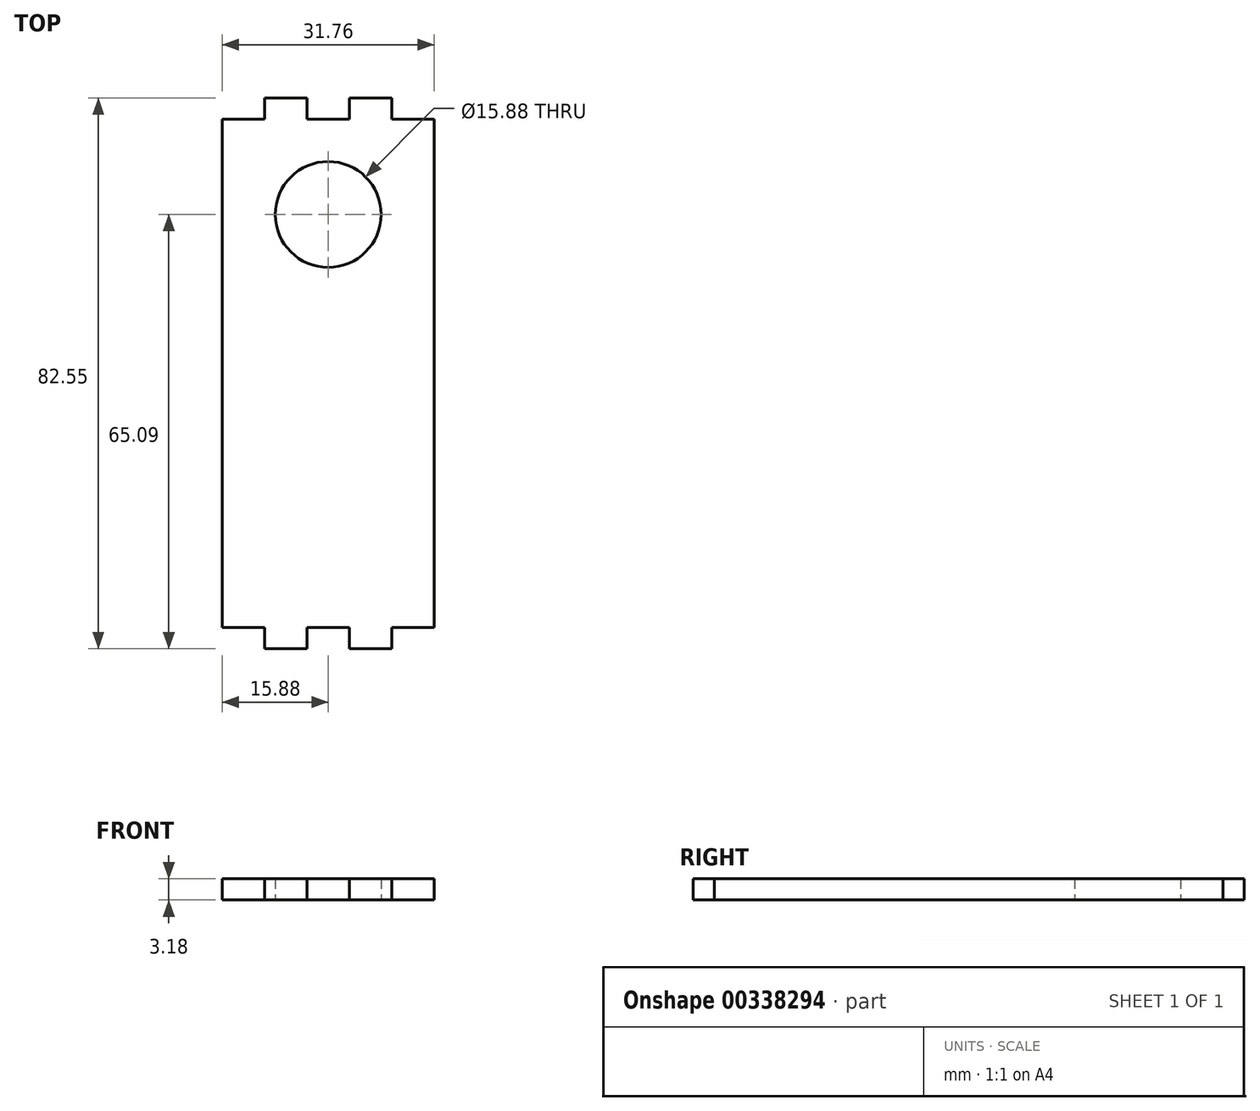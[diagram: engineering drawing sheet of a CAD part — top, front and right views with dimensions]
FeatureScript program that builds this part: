
annotation { "Feature Type Name" : "Feature", "Feature Type Description" : "" }
export const myFeature = defineFeature(function(context is Context, id is Id, definition is map)
    precondition{}
    {
        {
            var Q0;
            Q0=qCreatedBy(makeId("Top.planeOp"),FACE);
            var sketch = newSketch(context, id + "F0", { "sketchPlane" : qUnion([Q0])});
            skCircle(sketch, "E0", {"center": v(0, 0) * mm, "radius": 7.94 * mm});
            skLineSegment(sketch, "E1.bottom", {"start": v(-15.87, 17.46) * mm, "end": v(15.87, 17.46) * mm});
            skLineSegment(sketch, "E1.top", {"start": v(-15.87, -65.09) * mm, "end": v(15.87, -65.09) * mm});
            skLineSegment(sketch, "E1.left", {"start": v(-15.88, 17.46) * mm, "end": v(-15.87, -65.09) * mm});
            skLineSegment(sketch, "E1.right", {"start": v(15.88, 17.46) * mm, "end": v(15.88, -65.09) * mm});
            skLineSegment(sketch, "E2", {"start": v(0, 0) * mm, "end": v(0, 17.46) * mm, "construction": true});
            skSolve(sketch);
        }
        {
            var Q0;
            Q0=makeQuery(id+"F0.imprint","IMPRINT",FACE,{"disambiguationData":[TD([[makeQuery(id+"F0.imprint","IMPRINT",EDGE,{"derivedFrom":sQuery(id+"F0.wireOp",EDGE,"E0")}),-1.0]])]});
            extrude(context, id + "F1", {"entities" : qUnion([Q0]), "depth" : 3.17 * mm});
        }
        {
            var Q0;
            Q0=makeQuery(id+"F1.opExtrude","CAP_FACE",FACE,{"disambiguationData":[OSD([sQuery(id+"F0.wireOp",EDGE,"E0"),sQuery(id+"F0.wireOp",EDGE,"E1.bottom"),sQuery(id+"F0.wireOp",EDGE,"E1.top"),sQuery(id+"F0.wireOp",EDGE,"E1.left"),sQuery(id+"F0.wireOp",EDGE,"E1.right")])],"isStart":false});
            var sketch = newSketch(context, id + "F2", { "sketchPlane" : qUnion([Q0])});
            skLineSegment(sketch, "E3.bottom", {"start": v(-15.87, 17.46) * mm, "end": v(-9.52, 17.46) * mm});
            skLineSegment(sketch, "E3.top", {"start": v(-15.87, 14.29) * mm, "end": v(-9.52, 14.29) * mm});
            skLineSegment(sketch, "E3.left", {"start": v(-15.87, 17.46) * mm, "end": v(-15.87, 14.29) * mm});
            skLineSegment(sketch, "E3.right", {"start": v(-9.52, 17.46) * mm, "end": v(-9.52, 14.29) * mm});
            skLineSegment(sketch, "E4.bottom", {"start": v(-3.17, 17.46) * mm, "end": v(3.17, 17.46) * mm});
            skLineSegment(sketch, "E4.top", {"start": v(-3.17, 14.29) * mm, "end": v(3.17, 14.29) * mm});
            skLineSegment(sketch, "E4.left", {"start": v(-3.17, 17.46) * mm, "end": v(-3.17, 14.29) * mm});
            skLineSegment(sketch, "E4.right", {"start": v(3.17, 17.46) * mm, "end": v(3.17, 14.29) * mm});
            skLineSegment(sketch, "E5.bottom", {"start": v(15.87, 17.46) * mm, "end": v(9.52, 17.46) * mm});
            skLineSegment(sketch, "E5.top", {"start": v(15.87, 14.29) * mm, "end": v(9.52, 14.29) * mm});
            skLineSegment(sketch, "E5.left", {"start": v(15.87, 17.46) * mm, "end": v(15.87, 14.29) * mm});
            skLineSegment(sketch, "E5.right", {"start": v(9.52, 17.46) * mm, "end": v(9.52, 14.29) * mm});
            skLineSegment(sketch, "E6", {"start": v(-9.52, 14.29) * mm, "end": v(-3.17, 14.29) * mm, "construction": true});
            skLineSegment(sketch, "E7", {"start": v(3.17, 14.29) * mm, "end": v(9.52, 14.29) * mm, "construction": true});
            skLineSegment(sketch, "E8.bottom", {"start": v(-15.87, -65.09) * mm, "end": v(-9.52, -65.09) * mm});
            skLineSegment(sketch, "E8.top", {"start": v(-15.87, -61.91) * mm, "end": v(-9.52, -61.91) * mm});
            skLineSegment(sketch, "E8.left", {"start": v(-15.87, -65.09) * mm, "end": v(-15.87, -61.91) * mm});
            skLineSegment(sketch, "E8.right", {"start": v(-9.52, -65.09) * mm, "end": v(-9.52, -61.91) * mm});
            skLineSegment(sketch, "E9.bottom", {"start": v(15.88, -65.09) * mm, "end": v(9.53, -65.09) * mm});
            skLineSegment(sketch, "E9.top", {"start": v(15.88, -61.91) * mm, "end": v(9.53, -61.91) * mm});
            skLineSegment(sketch, "E9.left", {"start": v(15.88, -65.09) * mm, "end": v(15.88, -61.91) * mm});
            skLineSegment(sketch, "E9.right", {"start": v(9.53, -65.09) * mm, "end": v(9.53, -61.91) * mm});
            skLineSegment(sketch, "E10.bottom", {"start": v(-3.17, -65.09) * mm, "end": v(3.18, -65.09) * mm});
            skLineSegment(sketch, "E10.top", {"start": v(-3.17, -61.91) * mm, "end": v(3.18, -61.91) * mm});
            skLineSegment(sketch, "E10.left", {"start": v(-3.17, -65.09) * mm, "end": v(-3.17, -61.91) * mm});
            skLineSegment(sketch, "E10.right", {"start": v(3.18, -65.09) * mm, "end": v(3.18, -61.91) * mm});
            skLineSegment(sketch, "E11", {"start": v(-9.52, -61.91) * mm, "end": v(-3.17, -61.91) * mm, "construction": true});
            skLineSegment(sketch, "E12", {"start": v(3.18, -61.91) * mm, "end": v(9.53, -61.91) * mm, "construction": true});
            skSolve(sketch);
        }
        {
            var Q0;
            Q0 = qSketchRegion(id + "F2", true);
            var Q1;
            Q1=makeQuery(id+"F1.opExtrude","CAP_FACE",FACE,{"disambiguationData":[OSD([sQuery(id+"F0.wireOp",EDGE,"E0"),sQuery(id+"F0.wireOp",EDGE,"E1.bottom"),sQuery(id+"F0.wireOp",EDGE,"E1.top"),sQuery(id+"F0.wireOp",EDGE,"E1.left"),sQuery(id+"F0.wireOp",EDGE,"E1.right")])],"isStart":true});
            extrude(context, id + "F3", {"entities" : qUnion([Q0]), "operationType" : NewBodyOperationType.REMOVE, "endBound" : BoundingType.UP_TO_SURFACE, "oppositeDirection" : true, "endBoundEntityFace" : qUnion([Q1]), "depth" : 25.4 * mm});
        }
    });
